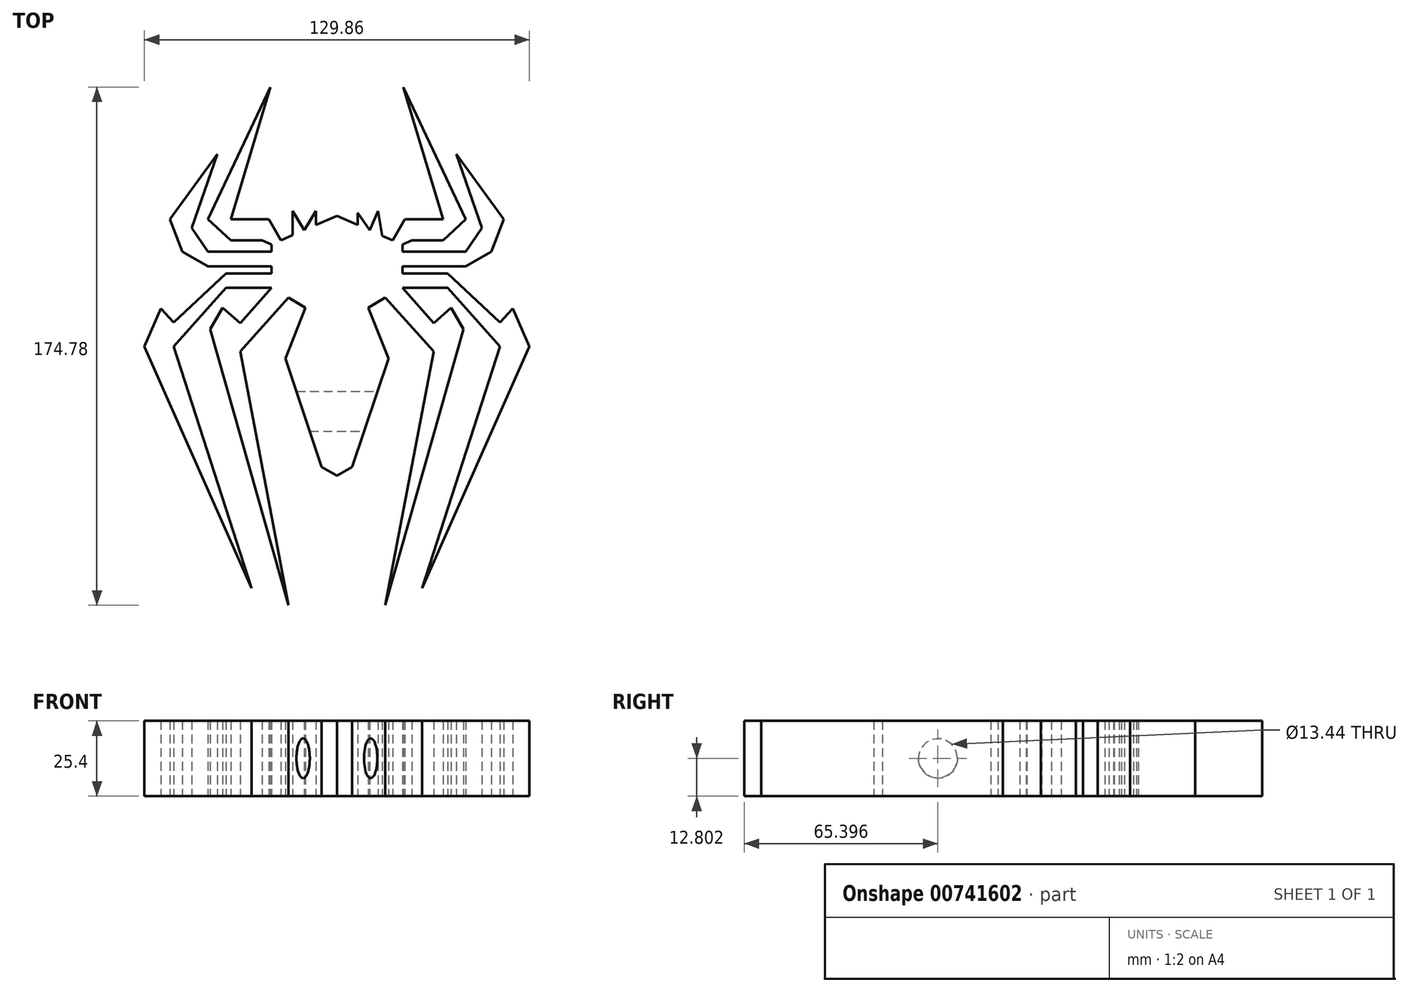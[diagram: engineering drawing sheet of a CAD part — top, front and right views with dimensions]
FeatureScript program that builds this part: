
annotation { "Feature Type Name" : "Feature", "Feature Type Description" : "" }
export const myFeature = defineFeature(function(context is Context, id is Id, definition is map)
    precondition{}
    {
        {
            var Q0;
            Q0=qCreatedBy(makeId("Top.planeOp"),FACE);
            var sketch = newSketch(context, id + "F0", { "sketchPlane" : qUnion([Q0])});
            skLineSegment(sketch, "E0", {"start": v(0, 30.98) * mm, "end": v(-22.08, 21.3) * mm});
            skLineSegment(sketch, "E1", {"start": v(-22.08, 21.3) * mm, "end": v(-22.08, 6.6) * mm});
            skLineSegment(sketch, "E2", {"start": v(-22.08, 6.6) * mm, "end": v(-10.63, 0) * mm});
            skLineSegment(sketch, "E3", {"start": v(-10.63, 0) * mm, "end": v(-17.39, -17.18) * mm});
            skLineSegment(sketch, "E4", {"start": v(-17.39, -17.18) * mm, "end": v(-5.12, -53.73) * mm});
            skLineSegment(sketch, "E5", {"start": v(-5.12, -53.73) * mm, "end": v(0, -56.69) * mm});
            skPoint(sketch, "E6", {"position": v(-18.87, 22.7) * mm});
            skLineSegment(sketch, "E7", {"start": v(-18.87, 22.7) * mm, "end": v(-22.9, 29.75) * mm});
            skLineSegment(sketch, "E8", {"start": v(-22.9, 29.75) * mm, "end": v(-35.82, 29.75) * mm});
            skLineSegment(sketch, "E9", {"start": v(-35.82, 29.75) * mm, "end": v(-22.42, 74.35) * mm});
            skLineSegment(sketch, "E10", {"start": v(-22.42, 74.35) * mm, "end": v(-43.5, 29.75) * mm});
            skLineSegment(sketch, "E11", {"start": v(-43.5, 29.75) * mm, "end": v(-35.82, 22.7) * mm});
            skLineSegment(sketch, "E12", {"start": v(-35.82, 22.7) * mm, "end": v(-25.27, 22.7) * mm});
            skLineSegment(sketch, "E13", {"start": v(-25.27, 22.7) * mm, "end": v(-22.08, 21.3) * mm});
            skPoint(sketch, "E14", {"position": v(-22.08, 18.87) * mm});
            skLineSegment(sketch, "E15", {"start": v(-22.08, 13.95) * mm, "end": v(-43.5, 13.95) * mm});
            skLineSegment(sketch, "E16", {"start": v(-43.5, 13.95) * mm, "end": v(-52.13, 18.87) * mm});
            skLineSegment(sketch, "E17", {"start": v(-52.13, 18.87) * mm, "end": v(-56.32, 29.75) * mm});
            skLineSegment(sketch, "E18", {"start": v(-56.32, 29.75) * mm, "end": v(-40.3, 51.81) * mm});
            skLineSegment(sketch, "E19", {"start": v(-40.3, 51.81) * mm, "end": v(-48.94, 26.87) * mm});
            skLineSegment(sketch, "E20", {"start": v(-48.94, 26.87) * mm, "end": v(-43.5, 18.87) * mm});
            skLineSegment(sketch, "E21", {"start": v(-43.5, 18.87) * mm, "end": v(-22.08, 18.87) * mm});
            skPoint(sketch, "E22", {"position": v(-22.08, 11.51) * mm});
            skLineSegment(sketch, "E23", {"start": v(-22.08, 11.51) * mm, "end": v(-37.42, 11.51) * mm});
            skLineSegment(sketch, "E24", {"start": v(-37.42, 11.51) * mm, "end": v(-55.01, -5) * mm});
            skLineSegment(sketch, "E25", {"start": v(-55.01, -5) * mm, "end": v(-59.38, -0.34) * mm});
            skLineSegment(sketch, "E26", {"start": v(-59.38, -0.34) * mm, "end": v(-64.93, -13.11) * mm});
            skLineSegment(sketch, "E27", {"start": v(-64.93, -13.11) * mm, "end": v(-28.79, -94.67) * mm});
            skLineSegment(sketch, "E28", {"start": v(-28.79, -94.67) * mm, "end": v(-55.01, -13.11) * mm});
            skLineSegment(sketch, "E29", {"start": v(-55.01, -13.11) * mm, "end": v(-37.42, 6.6) * mm});
            skLineSegment(sketch, "E30", {"start": v(-37.42, 6.6) * mm, "end": v(-22.08, 6.6) * mm});
            skPoint(sketch, "E31", {"position": v(-16.36, 3.3) * mm});
            skLineSegment(sketch, "E32", {"start": v(-22.08, 6.6) * mm, "end": v(-32.66, -5.24) * mm});
            skLineSegment(sketch, "E33", {"start": v(-32.66, -5.24) * mm, "end": v(-38.53, 0) * mm});
            skLineSegment(sketch, "E34", {"start": v(-38.53, 0) * mm, "end": v(-42.78, -7.35) * mm});
            skLineSegment(sketch, "E35", {"start": v(-42.78, -7.35) * mm, "end": v(-16.36, -100.43) * mm});
            skLineSegment(sketch, "E36", {"start": v(-16.36, -100.43) * mm, "end": v(-32.66, -14.8) * mm});
            skLineSegment(sketch, "E37", {"start": v(-32.66, -14.8) * mm, "end": v(-16.36, 3.3) * mm});
            skLineSegment(sketch, "E38.MirrorCS", {"start": v(25.27, 22.7) * mm, "end": v(22.08, 21.3) * mm});
            skLineSegment(sketch, "E39.MirrorCS", {"start": v(22.08, 21.3) * mm, "end": v(22.08, 6.6) * mm});
            skLineSegment(sketch, "E40.MirrorCS", {"start": v(43.5, 13.95) * mm, "end": v(52.13, 18.87) * mm});
            skLineSegment(sketch, "E41.MirrorCS", {"start": v(18.87, 22.7) * mm, "end": v(22.9, 29.75) * mm});
            skLineSegment(sketch, "E42.MirrorCS", {"start": v(48.94, 26.87) * mm, "end": v(43.5, 18.87) * mm});
            skLineSegment(sketch, "E43.MirrorCS", {"start": v(32.66, -5.24) * mm, "end": v(38.53, 0) * mm});
            skLineSegment(sketch, "E44.MirrorCS", {"start": v(22.08, 6.6) * mm, "end": v(10.63, 0) * mm});
            skLineSegment(sketch, "E45.MirrorCS", {"start": v(38.53, 0) * mm, "end": v(42.78, -7.35) * mm});
            skLineSegment(sketch, "E46.MirrorCS", {"start": v(55.01, -5) * mm, "end": v(59.38, -0.34) * mm});
            skLineSegment(sketch, "E47.MirrorCS", {"start": v(5.12, -53.73) * mm, "end": v(0, -56.69) * mm});
            skPoint(sketch, "E48.MirrorP", {"position": v(18.87, 22.7) * mm});
            skLineSegment(sketch, "E49.MirrorCS", {"start": v(37.42, 6.6) * mm, "end": v(22.08, 6.6) * mm});
            skLineSegment(sketch, "E50.MirrorCS", {"start": v(22.08, 13.95) * mm, "end": v(43.5, 13.95) * mm});
            skLineSegment(sketch, "E51.MirrorCS", {"start": v(56.32, 29.75) * mm, "end": v(40.3, 51.81) * mm});
            skLineSegment(sketch, "E52.MirrorCS", {"start": v(16.36, -100.43) * mm, "end": v(32.66, -14.8) * mm});
            skPoint(sketch, "E53.MirrorP", {"position": v(16.36, 3.3) * mm});
            skLineSegment(sketch, "E54.MirrorCS", {"start": v(22.9, 29.75) * mm, "end": v(35.82, 29.75) * mm});
            skLineSegment(sketch, "E55.MirrorCS", {"start": v(43.5, 18.87) * mm, "end": v(22.08, 18.87) * mm});
            skLineSegment(sketch, "E56.MirrorCS", {"start": v(59.38, -0.34) * mm, "end": v(64.93, -13.11) * mm});
            skLineSegment(sketch, "E57.MirrorCS", {"start": v(55.01, -13.11) * mm, "end": v(37.42, 6.6) * mm});
            skLineSegment(sketch, "E58.MirrorCS", {"start": v(17.39, -17.18) * mm, "end": v(5.12, -53.73) * mm});
            skLineSegment(sketch, "E59.MirrorCS", {"start": v(22.08, 6.6) * mm, "end": v(32.66, -5.24) * mm});
            skLineSegment(sketch, "E60.MirrorCS", {"start": v(22.42, 74.35) * mm, "end": v(43.5, 29.75) * mm});
            skLineSegment(sketch, "E61.MirrorCS", {"start": v(35.82, 29.75) * mm, "end": v(22.42, 74.35) * mm});
            skLineSegment(sketch, "E62.MirrorCS", {"start": v(64.93, -13.11) * mm, "end": v(28.79, -94.67) * mm});
            skLineSegment(sketch, "E63.MirrorCS", {"start": v(0, 30.98) * mm, "end": v(22.08, 21.3) * mm});
            skLineSegment(sketch, "E64.MirrorCS", {"start": v(52.13, 18.87) * mm, "end": v(56.32, 29.75) * mm});
            skLineSegment(sketch, "E65.MirrorCS", {"start": v(35.82, 22.7) * mm, "end": v(25.27, 22.7) * mm});
            skLineSegment(sketch, "E66.MirrorCS", {"start": v(22.08, 11.51) * mm, "end": v(37.42, 11.51) * mm});
            skLineSegment(sketch, "E67.MirrorCS", {"start": v(28.79, -94.67) * mm, "end": v(55.01, -13.11) * mm});
            skLineSegment(sketch, "E68.MirrorCS", {"start": v(43.5, 29.75) * mm, "end": v(35.82, 22.7) * mm});
            skPoint(sketch, "E69.MirrorP", {"position": v(22.08, 18.87) * mm});
            skLineSegment(sketch, "E70.MirrorCS", {"start": v(10.63, 0) * mm, "end": v(17.39, -17.18) * mm});
            skLineSegment(sketch, "E71.MirrorCS", {"start": v(42.78, -7.35) * mm, "end": v(16.36, -100.43) * mm});
            skPoint(sketch, "E72.MirrorP", {"position": v(22.08, 11.51) * mm});
            skLineSegment(sketch, "E73.MirrorCS", {"start": v(40.3, 51.81) * mm, "end": v(48.94, 26.87) * mm});
            skLineSegment(sketch, "E74.MirrorCS", {"start": v(32.66, -14.8) * mm, "end": v(16.36, 3.3) * mm});
            skLineSegment(sketch, "E75.MirrorCS", {"start": v(37.42, 11.51) * mm, "end": v(55.01, -5) * mm});
            skPoint(sketch, "E76", {"position": v(-11.04, 26.14) * mm});
            skPoint(sketch, "E77", {"position": v(11.04, 26.14) * mm});
            skLineSegment(sketch, "E78", {"start": v(-11.04, 26.14) * mm, "end": v(-14.94, 24.43) * mm});
            skLineSegment(sketch, "E79", {"start": v(-14.94, 24.43) * mm, "end": v(-14.94, 32.62) * mm});
            skLineSegment(sketch, "E80", {"start": v(-14.94, 32.62) * mm, "end": v(-11.04, 26.14) * mm});
            skLineSegment(sketch, "E81", {"start": v(11.04, 26.14) * mm, "end": v(13.89, 32.62) * mm});
            skPoint(sketch, "E82", {"position": v(15.33, 24.26) * mm});
            skLineSegment(sketch, "E83", {"start": v(13.89, 32.62) * mm, "end": v(15.33, 24.26) * mm});
            skPoint(sketch, "E84", {"position": v(-7.06, 27.89) * mm});
            skPoint(sketch, "E85", {"position": v(7.06, 27.89) * mm});
            skLineSegment(sketch, "E86", {"start": v(7.06, 27.89) * mm, "end": v(7.06, 31.98) * mm});
            skLineSegment(sketch, "E87", {"start": v(7.06, 31.98) * mm, "end": v(11.04, 26.14) * mm});
            skLineSegment(sketch, "E88", {"start": v(-11.04, 26.14) * mm, "end": v(-7.06, 32.62) * mm});
            skLineSegment(sketch, "E89", {"start": v(-7.06, 32.62) * mm, "end": v(-7.06, 27.89) * mm});
            skSolve(sketch);
        }
        {
            var Q0;
            {var subQ2=sQuery(id+"F0.wireOp",EDGE,"E7");Q0=makeQuery(id+"F0.imprint","IMPRINT",FACE,{"disambiguationData":[TD([[makeQuery(id+"F0.imprint","IMPRINT",EDGE,{"derivedFrom":subQ2}),1.0]])]});}
            var Q1;
            {var subQ0=sQuery(id+"F0.wireOp",EDGE,"E15");Q1=makeQuery(id+"F0.imprint","IMPRINT",FACE,{"disambiguationData":[TD([[makeQuery(id+"F0.imprint","IMPRINT",EDGE,{"derivedFrom":subQ0}),-1.0]])]});}
            var Q2;
            {var subQ0=sQuery(id+"F0.wireOp",EDGE,"E23");Q2=makeQuery(id+"F0.imprint","IMPRINT",FACE,{"disambiguationData":[TD([[makeQuery(id+"F0.imprint","IMPRINT",EDGE,{"derivedFrom":subQ0}),1.0]])]});}
            var Q3;
            {var subQ0=sQuery(id+"F0.wireOp",EDGE,"E32");Q3=makeQuery(id+"F0.imprint","IMPRINT",FACE,{"disambiguationData":[TD([[makeQuery(id+"F0.imprint","IMPRINT",EDGE,{"derivedFrom":subQ0}),1.0]])]});}
            var Q4;
            {var subQ0=sQuery(id+"F0.wireOp",EDGE,"E79");Q4=makeQuery(id+"F0.imprint","IMPRINT",FACE,{"disambiguationData":[TD([[makeQuery(id+"F0.imprint","IMPRINT",EDGE,{"derivedFrom":subQ0}),-1.0]])]});}
            var Q5;
            {var subQ2=sQuery(id+"F0.wireOp",EDGE,"E86");Q5=makeQuery(id+"F0.imprint","IMPRINT",FACE,{"disambiguationData":[TD([[makeQuery(id+"F0.imprint","IMPRINT",EDGE,{"derivedFrom":subQ2}),-1.0]])]});}
            var Q6;
            {var subQ6=sQuery(id+"F0.wireOp",EDGE,"E3");Q6=makeQuery(id+"F0.imprint","IMPRINT",FACE,{"disambiguationData":[TD([[makeQuery(id+"F0.imprint","IMPRINT",EDGE,{"derivedFrom":subQ6}),1.0]])]});}
            var Q7;
            {var subQ0=sQuery(id+"F0.wireOp",EDGE,"E88");Q7=makeQuery(id+"F0.imprint","IMPRINT",FACE,{"disambiguationData":[TD([[makeQuery(id+"F0.imprint","IMPRINT",EDGE,{"derivedFrom":subQ0}),-1.0]])]});}
            var Q8;
            {var subQ0=sQuery(id+"F0.wireOp",EDGE,"E81");Q8=makeQuery(id+"F0.imprint","IMPRINT",FACE,{"disambiguationData":[TD([[makeQuery(id+"F0.imprint","IMPRINT",EDGE,{"derivedFrom":subQ0}),-1.0]])]});}
            var Q9;
            {var subQ1=sQuery(id+"F0.wireOp",EDGE,"E38.MirrorCS");Q9=makeQuery(id+"F0.imprint","IMPRINT",FACE,{"disambiguationData":[TD([[makeQuery(id+"F0.imprint","IMPRINT",EDGE,{"derivedFrom":subQ1}),-1.0]])]});}
            var Q10;
            Q10=makeQuery(id+"F0.imprint","IMPRINT",FACE,{"disambiguationData":[TD([[makeQuery(id+"F0.imprint","IMPRINT",EDGE,{"derivedFrom":sQuery(id+"F0.wireOp",EDGE,"E40.MirrorCS")}),1.0]])]});
            var Q11;
            Q11=makeQuery(id+"F0.imprint","IMPRINT",FACE,{"disambiguationData":[TD([[makeQuery(id+"F0.imprint","IMPRINT",EDGE,{"derivedFrom":sQuery(id+"F0.wireOp",EDGE,"E46.MirrorCS")}),-1.0]])]});
            var Q12;
            Q12=makeQuery(id+"F0.imprint","IMPRINT",FACE,{"disambiguationData":[TD([[makeQuery(id+"F0.imprint","IMPRINT",EDGE,{"derivedFrom":sQuery(id+"F0.wireOp",EDGE,"E43.MirrorCS")}),-1.0]])]});
            extrude(context, id + "F1", {"entities" : qUnion([Q0, Q1, Q2, Q3, Q4, Q5, Q6, Q7, Q8, Q9, Q10, Q11, Q12]), "depth" : 25.4 * mm, "offsetDistance" : 25.4 * mm});
        }
        {
            var Q0;
            Q0=qCreatedBy(makeId("Right.planeOp"),FACE);
            var sketch = newSketch(context, id + "F2", { "sketchPlane" : qUnion([Q0])});
            skCircle(sketch, "E90", {"center": v(-35.03, 12.8) * mm, "radius": 6.72 * mm});
            skSolve(sketch);
        }
        {
            var Q0;
            Q0=makeQuery(id+"F2.imprint","IMPRINT",FACE,{"disambiguationData":[TD([[makeQuery(id+"F2.imprint","IMPRINT",EDGE,{"derivedFrom":sQuery(id+"F2.wireOp",EDGE,"E90")}),1.0]])]});
            extrude(context, id + "F3", {"entities" : qUnion([Q0]), "operationType" : NewBodyOperationType.REMOVE, "endBound" : BoundingType.SYMMETRIC, "oppositeDirection" : true, "depth" : 38.6 * mm, "offsetDistance" : 25.4 * mm});
        }
    });
